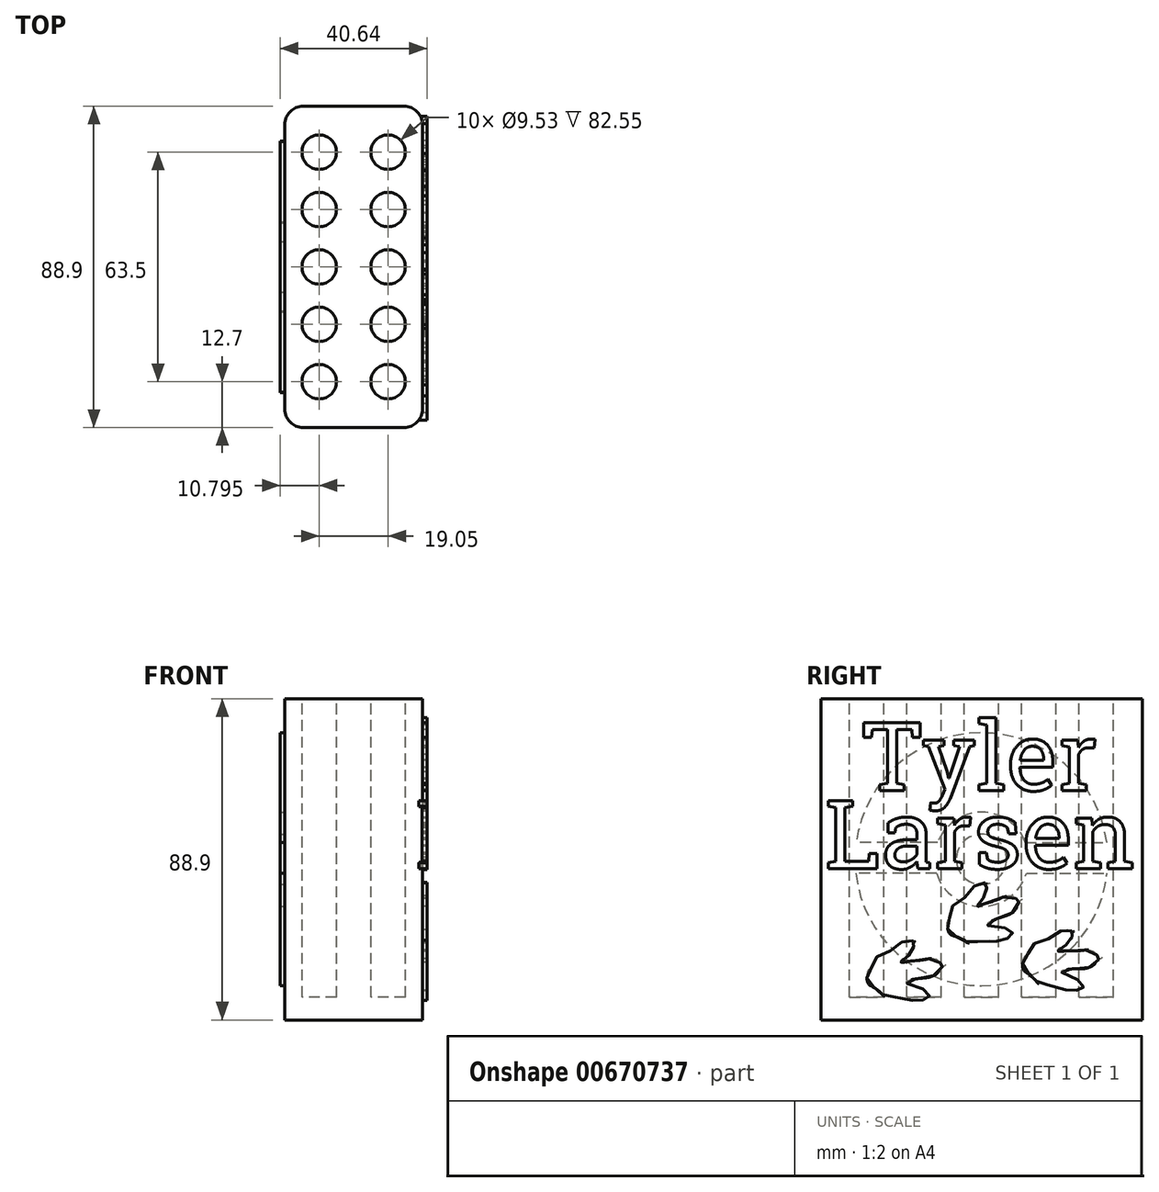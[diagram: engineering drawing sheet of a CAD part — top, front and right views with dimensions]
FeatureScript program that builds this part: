
annotation { "Feature Type Name" : "Feature", "Feature Type Description" : "" }
export const myFeature = defineFeature(function(context is Context, id is Id, definition is map)
    precondition{}
    {
        {
            var Q0;
            Q0=qCreatedBy(makeId("Right.planeOp"),FACE);
            var sketch = newSketch(context, id + "F0", { "sketchPlane" : qUnion([Q0])});
            skLineSegment(sketch, "E0.bottom", {"start": v(-44.45, 44.45) * mm, "end": v(44.45, 44.45) * mm});
            skLineSegment(sketch, "E0.top", {"start": v(-44.45, -44.45) * mm, "end": v(44.45, -44.45) * mm});
            skLineSegment(sketch, "E0.left", {"start": v(-44.45, 44.45) * mm, "end": v(-44.45, -44.45) * mm});
            skLineSegment(sketch, "E0.right", {"start": v(44.45, 44.45) * mm, "end": v(44.45, -44.45) * mm});
            skPoint(sketch, "E0.middle", {"position": v(0, 0) * mm});
            skSolve(sketch);
        }
        {
            var Q0;
            Q0=qSketchRegion(id+"F0",true);
            extrude(context, id + "F1", {"entities" : qUnion([Q0]), "endBound" : BoundingType.SYMMETRIC, "depth" : 38.1 * mm, "offsetDistance" : 25.4 * mm});
        }
        {
            var Q0;
            Q0=makeQuery(id+"F1.opExtrude","SWEPT_FACE",FACE,{"disambiguationData":[OSD([sQuery(id+"F0.wireOp",EDGE,"E0.bottom")])]});
            var sketch = newSketch(context, id + "F2", { "sketchPlane" : qUnion([Q0])});
            skCircle(sketch, "E1", {"center": v(-9.52, -31.75) * mm, "radius": 4.76 * mm});
            skCircle(sketch, "E2", {"center": v(-9.52, 0) * mm, "radius": 4.76 * mm});
            skCircle(sketch, "E3", {"center": v(-9.52, -15.88) * mm, "radius": 4.76 * mm});
            skCircle(sketch, "E4", {"center": v(-9.52, 15.88) * mm, "radius": 4.76 * mm});
            skCircle(sketch, "E5", {"center": v(-9.52, 31.75) * mm, "radius": 4.76 * mm});
            skCircle(sketch, "E6.MirrorC", {"center": v(9.52, 0) * mm, "radius": 4.76 * mm});
            skCircle(sketch, "E7.MirrorC", {"center": v(9.52, -31.75) * mm, "radius": 4.76 * mm});
            skCircle(sketch, "E8.MirrorC", {"center": v(9.52, -15.88) * mm, "radius": 4.76 * mm});
            skCircle(sketch, "E9.MirrorC", {"center": v(9.52, 15.88) * mm, "radius": 4.76 * mm});
            skCircle(sketch, "E10.MirrorC", {"center": v(9.52, 31.75) * mm, "radius": 4.76 * mm});
            skSolve(sketch);
        }
        {
            var Q0;
            Q0=qSketchRegion(id+"F2",true);
            extrude(context, id + "F3", {"entities" : qUnion([Q0]), "operationType" : NewBodyOperationType.REMOVE, "oppositeDirection" : true, "depth" : 82.55 * mm, "offsetDistance" : 25.4 * mm});
        }
        {
            var Q0;
            Q0=makeQuery(id+"F1.opExtrude","CAP_FACE",FACE,{"disambiguationData":[OSD([sQuery(id+"F0.wireOp",EDGE,"E0.bottom"),sQuery(id+"F0.wireOp",EDGE,"E0.top"),sQuery(id+"F0.wireOp",EDGE,"E0.left"),sQuery(id+"F0.wireOp",EDGE,"E0.right")])],"isStart":false});
            var sketch = newSketch(context, id + "F4", { "sketchPlane" : qUnion([Q0])});
            skText(sketch, "E11", { "text": "Tyler", "fontName": "RobotoSlab-Regular.ttf"});
            skText(sketch, "E12", { "text": "Larsen", "fontName": "RobotoSlab-Regular.ttf"});
            const initialGuessF4  = {"E11": [-0.03307, 0.01905, 1, 0, 0.01905], "E12": [-0.04335, -0.00254, 1, 0, 0.01905]};
            skSetInitialGuess(sketch, initialGuessF4);
            skSolve(sketch);
        }
        {
            var Q0;
            Q0=qSketchRegion(id+"F4",true);
            extrude(context, id + "F5", {"entities" : qUnion([Q0]), "operationType" : NewBodyOperationType.ADD, "depth" : 1.27 * mm, "offsetDistance" : 25.4 * mm});
        }
        {
            var Q0;
            Q0=makeQuery(id+"F1.opExtrude","CAP_EDGE",EDGE,{"disambiguationData":[OSD([sQuery(id+"F0.wireOp",EDGE,"E0.left")])],"isStart":false});
            var Q1;
            Q1=makeQuery(id+"F1.opExtrude","CAP_EDGE",EDGE,{"disambiguationData":[OSD([sQuery(id+"F0.wireOp",EDGE,"E0.right")])],"isStart":false});
            var Q2;
            Q2=makeQuery(id+"F1.opExtrude","CAP_EDGE",EDGE,{"disambiguationData":[OSD([sQuery(id+"F0.wireOp",EDGE,"E0.right")])],"isStart":true});
            var Q3;
            Q3=makeQuery(id+"F1.opExtrude","CAP_EDGE",EDGE,{"disambiguationData":[OSD([sQuery(id+"F0.wireOp",EDGE,"E0.left")])],"isStart":true});
            fillet(context, id + "F6", {"entities" : qUnion([Q0, Q1, Q2, Q3]), "radius" : 5.08 * mm, "tangentPropagation" : true, "allowEdgeOverflow" : false});
        }
        {
            var Q0;
            {var subQ0=sQuery(id+"F0.wireOp",EDGE,"E0.right");var subQ1=sQuery(id+"F0.wireOp",EDGE,"E0.left");var subQ2=sQuery(id+"F0.wireOp",EDGE,"E0.top");var subQ3=sQuery(id+"F0.wireOp",EDGE,"E0.bottom");Q0=makeQuery(id+"F5.boolean.opBoolean","SPLIT",FACE,{"disambiguationData":[TD([makeQuery(id+"F1.opExtrude","SWEPT_FACE",FACE,{"disambiguationData":[OSD([subQ3])]})])],"derivedFrom":makeQuery(id+"F1.opExtrude","CAP_FACE",FACE,{"disambiguationData":[OSD([subQ3,subQ2,subQ1,subQ0])],"isStart":false})});}
            var sketch = newSketch(context, id + "F7", { "sketchPlane" : qUnion([Q0])});
            skFitSpline(sketch, "E13", {"points": [v(-31.68, -32.84) * mm, v(-31.5, -31.38) * mm, v(-30.97, -30.4) * mm, v(-30.23, -29.62) * mm, v(-29.6, -28.32) * mm, v(-29.16, -27.24) * mm, v(-28.19, -26.49) * mm, v(-26.53, -25.9) * mm, v(-24.31, -24.81) * mm, v(-22.86, -23.53) * mm, v(-21.58, -22.64) * mm, v(-19.9, -22.37) * mm, v(-19.5, -22.51) * mm, v(-18.8, -22.54) * mm, v(-18.43, -22.6) * mm, v(-18.56, -23.12) * mm, v(-18.83, -23.64) * mm, v(-18.71, -24.32) * mm, v(-19.15, -25.23) * mm, v(-19.82, -25.87) * mm, v(-20.27, -26.72) * mm, v(-21.3, -27.42) * mm, v(-22.24, -27.93) * mm, v(-22.26, -28.46) * mm, v(-21.7, -28.5) * mm, v(-20.28, -28.25) * mm, v(-17.7, -28) * mm, v(-15.52, -27.7) * mm, v(-14.38, -27.48) * mm, v(-12.27, -27.78) * mm, v(-11.57, -28.6) * mm, v(-10.42, -28.78) * mm, v(-9.84, -29.08) * mm, v(-10.69, -29.7) * mm, v(-11.33, -30.28) * mm, v(-12, -31.3) * mm, v(-13.66, -32.4) * mm, v(-16.71, -32.92) * mm, v(-19.9, -33.49) * mm, v(-20.84, -34.03) * mm, v(-20.99, -34.15) * mm, v(-20.65, -34.3) * mm, v(-18.33, -35.1) * mm, v(-15.87, -36.07) * mm, v(-15.2, -36.81) * mm, v(-15.13, -37.34) * mm, v(-14.42, -37.76) * mm, v(-14.42, -38.1) * mm, v(-15.22, -38.35) * mm, v(-15.6, -38.57) * mm, v(-15.93, -38.82) * mm, v(-17.04, -38.9) * mm, v(-17.75, -39.03) * mm, v(-18.84, -39.07) * mm, v(-21.56, -38.42) * mm, v(-24.88, -38.03) * mm, v(-26.21, -37.98) * mm, v(-27.2, -37.69) * mm, v(-27.84, -36.93) * mm, v(-28.71, -36.23) * mm, v(-29.46, -35.6) * mm, v(-30.49, -35.1) * mm, v(-31.33, -34.4) * mm, v(-31.68, -32.84) * mm]});
            skFitSpline(sketch, "E14", {"points": [v(-9.35, -19.25) * mm, v(-9.48, -17.78) * mm, v(-9.17, -16.72) * mm, v(-8.61, -15.8) * mm, v(-8.27, -14.38) * mm, v(-8.08, -13.24) * mm, v(-7.28, -12.3) * mm, v(-5.79, -11.38) * mm, v(-3.85, -9.84) * mm, v(-2.7, -8.28) * mm, v(-1.64, -7.13) * mm, v(-0.05, -6.52) * mm, v(0.36, -6.57) * mm, v(1.04, -6.45) * mm, v(1.43, -6.42) * mm, v(1.42, -6.97) * mm, v(1.26, -7.53) * mm, v(1.52, -8.17) * mm, v(1.28, -9.15) * mm, v(0.76, -9.92) * mm, v(0.5, -10.84) * mm, v(-0.36, -11.75) * mm, v(-1.17, -12.45) * mm, v(-1.07, -12.96) * mm, v(-0.52, -12.88) * mm, v(0.82, -12.34) * mm, v(3.3, -11.55) * mm, v(5.35, -10.79) * mm, v(6.42, -10.33) * mm, v(8.54, -10.19) * mm, v(9.4, -10.83) * mm, v(10.57, -10.77) * mm, v(11.2, -10.93) * mm, v(10.5, -11.72) * mm, v(10, -12.42) * mm, v(9.56, -13.55) * mm, v(8.16, -14.99) * mm, v(5.3, -16.15) * mm, v(2.3, -17.38) * mm, v(1.5, -18.11) * mm, v(1.38, -18.26) * mm, v(1.74, -18.34) * mm, v(4.18, -18.62) * mm, v(6.79, -19.05) * mm, v(7.6, -19.63) * mm, v(7.78, -20.13) * mm, v(8.56, -20.4) * mm, v(8.63, -20.72) * mm, v(7.9, -21.14) * mm, v(7.58, -21.44) * mm, v(7.31, -21.75) * mm, v(6.24, -22.07) * mm, v(5.58, -22.34) * mm, v(4.52, -22.61) * mm, v(1.73, -22.56) * mm, v(-1.6, -22.88) * mm, v(-2.92, -23.1) * mm, v(-3.93, -23.03) * mm, v(-4.73, -22.43) * mm, v(-5.73, -21.93) * mm, v(-6.6, -21.47) * mm, v(-7.7, -21.21) * mm, v(-8.67, -20.7) * mm, v(-9.35, -19.25) * mm]});
            skFitSpline(sketch, "E15", {"points": [v(11.39, -28.93) * mm, v(11.7, -27.49) * mm, v(12.31, -26.57) * mm, v(13.12, -25.85) * mm, v(13.87, -24.6) * mm, v(14.39, -23.57) * mm, v(15.43, -22.9) * mm, v(17.13, -22.47) * mm, v(19.43, -21.58) * mm, v(21, -20.42) * mm, v(22.35, -19.65) * mm, v(24.05, -19.53) * mm, v(24.42, -19.7) * mm, v(25.11, -19.79) * mm, v(25.49, -19.88) * mm, v(25.32, -20.4) * mm, v(25, -20.89) * mm, v(25.06, -21.58) * mm, v(24.54, -22.44) * mm, v(23.82, -23.02) * mm, v(23.3, -23.83) * mm, v(22.2, -24.43) * mm, v(21.22, -24.86) * mm, v(21.16, -25.38) * mm, v(21.71, -25.47) * mm, v(23.15, -25.35) * mm, v(25.75, -25.33) * mm, v(27.94, -25.21) * mm, v(29.1, -25.1) * mm, v(31.17, -25.59) * mm, v(31.8, -26.45) * mm, v(32.93, -26.74) * mm, v(33.47, -27.08) * mm, v(32.58, -27.63) * mm, v(31.89, -28.15) * mm, v(31.14, -29.1) * mm, v(29.38, -30.05) * mm, v(26.3, -30.31) * mm, v(23.07, -30.6) * mm, v(22.09, -31.06) * mm, v(21.93, -31.17) * mm, v(22.26, -31.35) * mm, v(24.5, -32.34) * mm, v(26.86, -33.52) * mm, v(27.46, -34.33) * mm, v(27.49, -34.86) * mm, v(28.15, -35.34) * mm, v(28.13, -35.67) * mm, v(27.3, -35.86) * mm, v(26.91, -36.04) * mm, v(26.56, -36.26) * mm, v(25.45, -36.25) * mm, v(24.73, -36.3) * mm, v(23.64, -36.26) * mm, v(20.99, -35.37) * mm, v(17.72, -34.7) * mm, v(16.4, -34.52) * mm, v(15.44, -34.15) * mm, v(14.86, -33.34) * mm, v(14.06, -32.56) * mm, v(13.36, -31.87) * mm, v(12.38, -31.3) * mm, v(11.6, -30.52) * mm, v(11.39, -28.93) * mm]});
            skSolve(sketch);
        }
        {
            var Q0;
            Q0=qSketchRegion(id+"F7",true);
            extrude(context, id + "F8", {"entities" : qUnion([Q0]), "operationType" : NewBodyOperationType.ADD, "depth" : 1.27 * mm, "offsetDistance" : 25.4 * mm});
        }
        {
            var Q0;
            Q0=makeQuery(id+"F1.opExtrude","CAP_FACE",FACE,{"disambiguationData":[OSD([sQuery(id+"F0.wireOp",EDGE,"E0.bottom"),sQuery(id+"F0.wireOp",EDGE,"E0.top"),sQuery(id+"F0.wireOp",EDGE,"E0.left"),sQuery(id+"F0.wireOp",EDGE,"E0.right")])],"isStart":true});
            var sketch = newSketch(context, id + "F9", { "sketchPlane" : qUnion([Q0])});
            skCircle(sketch, "E16", {"center": v(0, 0) * mm, "radius": 6.95 * mm});
            skCircle(sketch, "E17", {"center": v(0, 0) * mm, "radius": 13.03 * mm});
            skCircle(sketch, "E18", {"center": v(0, 0) * mm, "radius": 34.99 * mm});
            skLineSegment(sketch, "E19", {"start": v(-12.16, 4.68) * mm, "end": v(-34.67, 4.68) * mm});
            skLineSegment(sketch, "E20", {"start": v(-12.43, -3.91) * mm, "end": v(-34.77, -3.91) * mm});
            skLineSegment(sketch, "E21", {"start": v(12.16, 4.68) * mm, "end": v(34.67, 4.68) * mm});
            skLineSegment(sketch, "E22", {"start": v(12.43, -3.91) * mm, "end": v(34.77, -3.91) * mm});
            skLineSegment(sketch, "E23", {"start": v(34.77, -3.91) * mm, "end": v(35.89, -4.76) * mm});
            skSolve(sketch);
        }
        {
            var Q0;
            {var subQ0=sQuery(id+"F9.wireOp",EDGE,"E19");Q0=makeQuery(id+"F9.imprint","IMPRINT",FACE,{"disambiguationData":[TD([[makeQuery(id+"F9.imprint","IMPRINT",EDGE,{"derivedFrom":subQ0}),-1.0]])]});}
            var Q1;
            Q1=makeQuery(id+"F9.imprint","IMPRINT",FACE,{"disambiguationData":[TD([[makeQuery(id+"F9.imprint","IMPRINT",EDGE,{"derivedFrom":sQuery(id+"F9.wireOp",EDGE,"E16")}),1.0]])]});
            var Q2;
            {var subQ0=sQuery(id+"F9.wireOp",EDGE,"E20");Q2=makeQuery(id+"F9.imprint","IMPRINT",FACE,{"disambiguationData":[TD([[makeQuery(id+"F9.imprint","IMPRINT",EDGE,{"derivedFrom":subQ0}),1.0]])]});}
            extrude(context, id + "F10", {"entities" : qUnion([Q0, Q1, Q2]), "operationType" : NewBodyOperationType.ADD, "depth" : 1.27 * mm, "offsetDistance" : 25.4 * mm});
        }
    });
